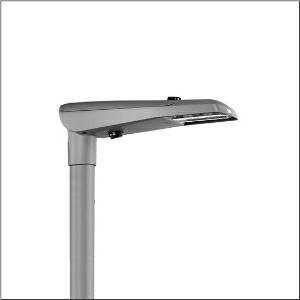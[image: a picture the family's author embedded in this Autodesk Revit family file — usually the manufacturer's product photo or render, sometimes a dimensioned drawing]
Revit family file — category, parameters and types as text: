
# Revit family: streetlight_sl_11_iq_micro___st1_2a_5xc1ac1y08ce_2333
name_source: partatom
category: Lighting Fixtures
units: mm (PartAtom-declared; Revit-internal decimal feet)

## family parameters
Cut with Voids When Loaded = No
Host = Face
Light Source = No
Part Type = Normal
Room Calculation Point = No
Round Connector Dimension = Use Diameter
Shared = No

## types (1)
- --- (1 x LED, 1600 lm, 14 W, 2200K)
    Apparent Load = 14 VA
    CIE Flux Codes = 33 71 96 100 100
    Color Rendering = 70
    Color Temperature = 2200K
    Default Elevation = 1800 mm
    Description = Streetlight SL 11 iQ micro, mast luminaire, primary light control with 3 zone facetted reflector, of plastic, silver coated, highly specular, primary optical cover: cover, of PMMA, transparent, light distribution: ST1.2a, light emission: direct distribution, primary light characteristic: asymmetric, installation type: post-top, side-entry, lamps: LED, High Power LED, rated values: 1.880lm | 13,8W | 136,2lm/W (begin service life); end service life: 1.880lm | 14W; at 50% lumin. flux: 940lm | 7,5W | 125,3lm/W, colour temperature: 2200/2700/3000/4000K, colour rendering: CRI > 70, light colour: 722/727/730/740, light setting 1 begin service life: 100% | 1.880lm | 13,8W | 136,2lm/W | 3.000K, light setting 1 end service life: 14W, further light settings possible, control: pre-setting: logarithmic dimming characteristic, Street-Remote, Auto-Match, Temp-Guard, Lumen-Switch, Night-Set, Smart-Wire, Light-Fading, Desk-Remote (wireless, voltage-free reading and setting of iQ features in the workshop via application-optimized NFC function/RFID function), optimised constant luminous flux control (CLO 2.0), with cable H07RN-F 5x 1.5mm², mains connection: 220..240V, AC, 50/60Hz, connection cable pre-assembled, cable length: 5,5m, luminaire housing, of diecast aluminium, powder-coated, Siteco® metallic grey (DB 702S), please order mast flange separately, inclination adjustable without tools: 0°, 5°, 10°, 15° (post-top) | 0°, -5°, -10°, -15° (side-entry), sealing non-destructively replaceable, multi-level sealing system, length: 600mm, width: 174mm, height: 116mm, mast flange for spigot size: 42mm (side-entry): 5XC10008XM4, 60/48mm (side-entry/post-top): 5XC10108XM2, 76/60mm (side-entry/post-top): 5XC10108XM1, equipment: standard, Smart Interface below and above, protection rating (complete): IP66, insulation class (complete): insulation class II (safety insulation), certification: CE, ENEC, ENEC+, VDE, UKCA, impact resistance: IK10, permissible operating ambient temperature for outdoor applications: -25..+50°C, standard-compliant lighting for roads and squares, Environmental Product Declaration (EPD) tested and certified by an independent institute, packaging unit: 1 piece

Light Distribution: ST1.2a
    Height = 116 mm
    Lamp = 1 x LED
    Lamp Light Flux = 1600 lm
    Lamp Power = 14 W
    Lamp count = 1
    Length = 600 mm
    Luminous efficacy = 114 lm/W
    Manufacturer = Siteco
    ModVariant = No
    Model = 5XC1AC1Y08CE
    Number of Poles = 1
    OnlyDefault = Yes
    Power Factor = 1
    Product Name = Streetlight SL 11 iQ micro | ST1.2a
    Product group = mast luminaire | pylon top
    ProductGroupID = 6100
    Protection Class = Protection class II
    Protection Degree = IP 66
    RLX_Detail_Level = 1
    RLX_Emergency_Light_Flux = 0 lm
    RLX_Emergency_Type = 0
    RLX_Emergency_Type_DB = No
    RlxData = <blob elided: 59149 chars, md5=1c1fd4bf>
    Socket = socket
    Standby Power = 0 W
    System Light Flux = 1600 lm
    System Power = 14 W
    Type Comments = individual setting: luminous flux: 100 % | dim-lin: 254 | 369 mA
    Type Image = l_1005956.jpg
    URL = http://relux.com
    VarID = @adj_035148
    Voltage = 0 V
    Weight = 0.00 kg
    Width = 174 mm

## geometry (parser evidence)
native form markers: Blend x4, Sweep x12
no freeform markers — native parametric forms only
